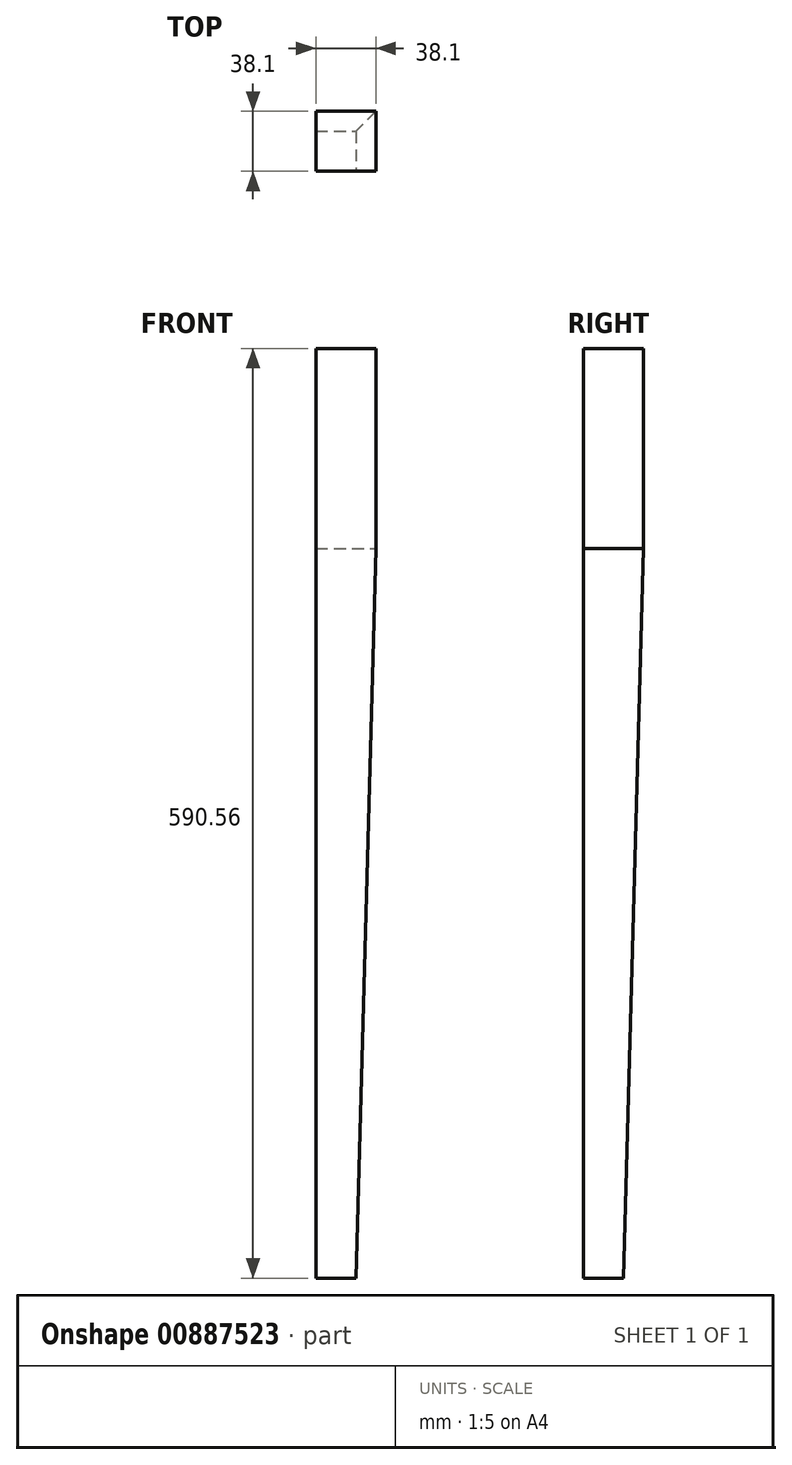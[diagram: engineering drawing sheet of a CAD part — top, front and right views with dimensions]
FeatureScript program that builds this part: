
annotation { "Feature Type Name" : "Feature", "Feature Type Description" : "" }
export const myFeature = defineFeature(function(context is Context, id is Id, definition is map)
    precondition{}
    {
        {
            var Q0;
            Q0=qCreatedBy(makeId("Front.planeOp"),FACE);
            var sketch = newSketch(context, id + "F0", { "sketchPlane" : qUnion([Q0])});
            skLineSegment(sketch, "E0.bottom", {"start": v(19.05, 295.28) * mm, "end": v(-19.05, 295.28) * mm});
            skLineSegment(sketch, "E0.top", {"start": v(19.05, -295.28) * mm, "end": v(-19.05, -295.28) * mm});
            skLineSegment(sketch, "E0.left", {"start": v(19.05, 295.28) * mm, "end": v(19.05, -295.28) * mm});
            skLineSegment(sketch, "E0.right", {"start": v(-19.05, 295.28) * mm, "end": v(-19.05, -295.28) * mm});
            skPoint(sketch, "E0.middle", {"position": v(0, 0) * mm});
            skSolve(sketch);
        }
        {
            var Q0;
            Q0=makeQuery(id+"F0.imprint","IMPRINT",FACE,{"disambiguationData":[TD([[makeQuery(id+"F0.imprint","IMPRINT",EDGE,{"derivedFrom":sQuery(id+"F0.wireOp",EDGE,"E0.bottom")}),1.0]])]});
            extrude(context, id + "F1", {"entities" : qUnion([Q0]), "endBound" : BoundingType.SYMMETRIC, "depth" : 38.1 * mm, "offsetDistance" : 25.4 * mm});
        }
        {
            var Q0;
            Q0=makeQuery(id+"F1.opExtrude","CAP_FACE",FACE,{"disambiguationData":[OSD([sQuery(id+"F0.wireOp",EDGE,"E0.bottom"),sQuery(id+"F0.wireOp",EDGE,"E0.top"),sQuery(id+"F0.wireOp",EDGE,"E0.left"),sQuery(id+"F0.wireOp",EDGE,"E0.right")])],"isStart":false});
            var sketch = newSketch(context, id + "F2", { "sketchPlane" : qUnion([Q0])});
            skLineSegment(sketch, "E1", {"start": v(6.35, -295.28) * mm, "end": v(19.05, -295.28) * mm});
            skLineSegment(sketch, "E2", {"start": v(19.05, -295.28) * mm, "end": v(19.05, 168.28) * mm});
            skLineSegment(sketch, "E3", {"start": v(19.05, 168.28) * mm, "end": v(6.35, -295.28) * mm});
            skSolve(sketch);
        }
        {
            var Q0;
            Q0=makeQuery(id+"F2.imprint","IMPRINT",FACE,{"disambiguationData":[TD([[makeQuery(id+"F2.imprint","IMPRINT",EDGE,{"derivedFrom":sQuery(id+"F2.wireOp",EDGE,"E1")}),-1.0]])]});
            extrude(context, id + "F3", {"entities" : qUnion([Q0]), "operationType" : NewBodyOperationType.REMOVE, "endBound" : BoundingType.UP_TO_NEXT, "oppositeDirection" : true, "depth" : 25.4 * mm, "offsetDistance" : 25.4 * mm});
        }
        {
            var Q0;
            Q0=makeQuery(id+"F1.opExtrude","SWEPT_FACE",FACE,{"disambiguationData":[OSD([sQuery(id+"F0.wireOp",EDGE,"E0.left")])]});
            var sketch = newSketch(context, id + "F4", { "sketchPlane" : qUnion([Q0])});
            skLineSegment(sketch, "E4.0", {"start": v(19.05, -295.28) * mm, "end": v(-19.05, -295.28) * mm, "construction": true});
            skLineSegment(sketch, "E5", {"start": v(19.05, 168.28) * mm, "end": v(19.05, -295.28) * mm});
            skLineSegment(sketch, "E6", {"start": v(6.35, -295.28) * mm, "end": v(19.05, -295.28) * mm});
            skLineSegment(sketch, "E7", {"start": v(6.35, -295.28) * mm, "end": v(19.05, 168.28) * mm});
            skSolve(sketch);
        }
        {
            var Q0;
            Q0=makeQuery(id+"F4.imprint","IMPRINT",FACE,{"disambiguationData":[TD([[makeQuery(id+"F4.imprint","IMPRINT",EDGE,{"derivedFrom":sQuery(id+"F4.wireOp",EDGE,"E5")}),-1.0]])]});
            extrude(context, id + "F5", {"entities" : qUnion([Q0]), "operationType" : NewBodyOperationType.REMOVE, "endBound" : BoundingType.THROUGH_ALL, "oppositeDirection" : true, "depth" : 25.4 * mm, "offsetDistance" : 25.4 * mm});
        }
    });
